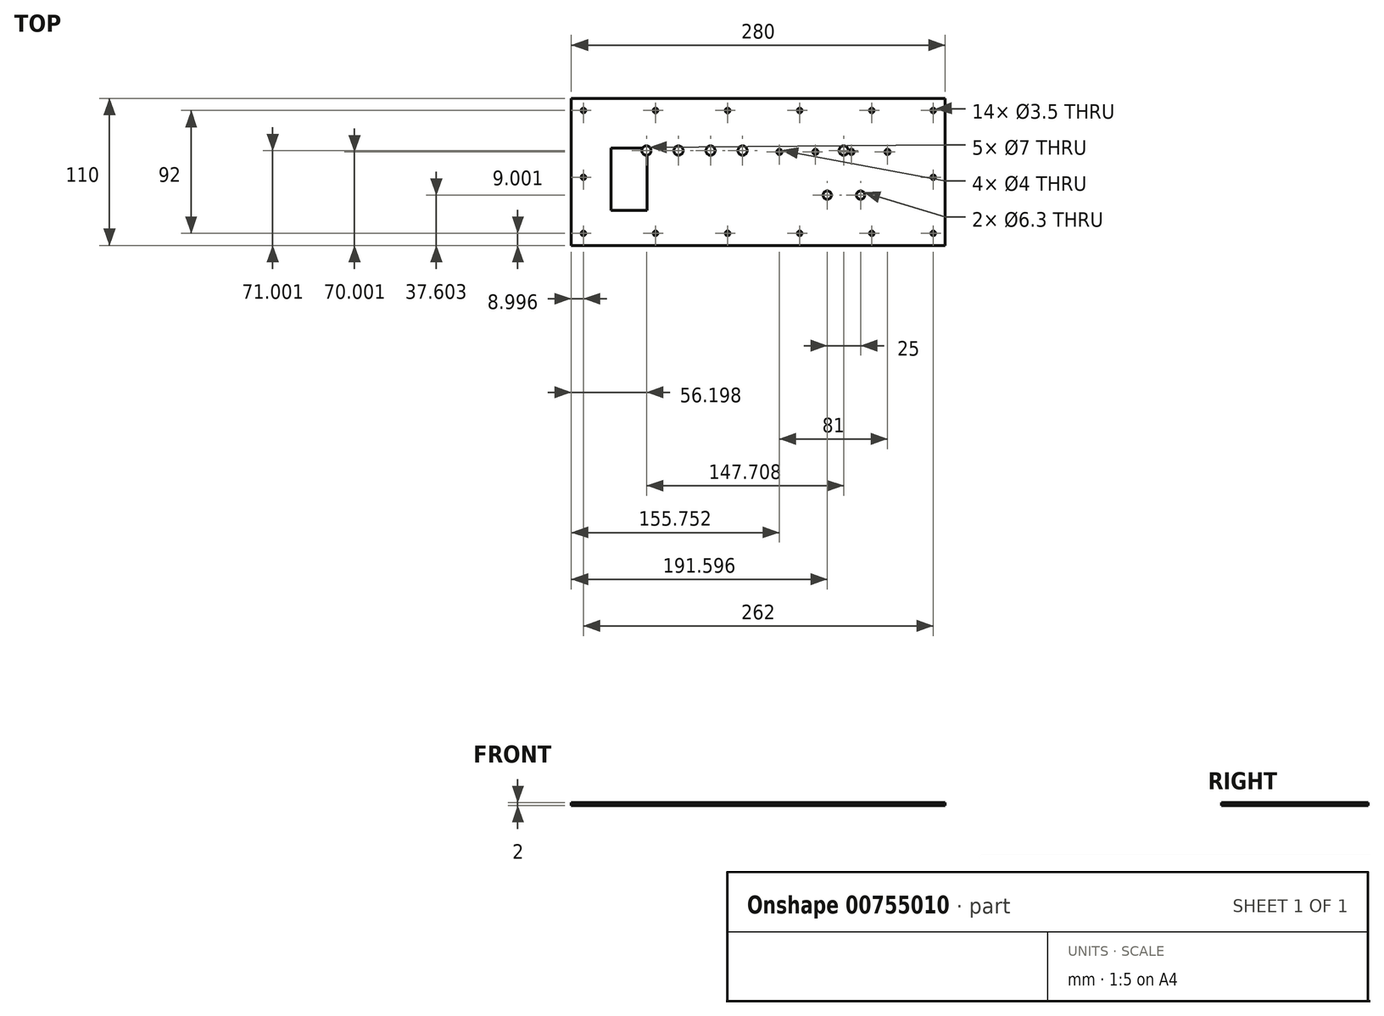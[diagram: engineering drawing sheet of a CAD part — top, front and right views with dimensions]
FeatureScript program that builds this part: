
annotation { "Feature Type Name" : "Feature", "Feature Type Description" : "" }
export const myFeature = defineFeature(function(context is Context, id is Id, definition is map)
    precondition{}
    {
        {
            var Q0;
            Q0=qCreatedBy(makeId("Top.planeOp"),FACE);
            var sketch = newSketch(context, id + "F0", { "sketchPlane" : qUnion([Q0])});
            skLineSegment(sketch, "E0.bottom", {"start": v(-230.24, 76.32) * mm, "end": v(49.76, 76.32) * mm});
            skLineSegment(sketch, "E0.top", {"start": v(-230.24, -33.68) * mm, "end": v(49.76, -33.68) * mm});
            skLineSegment(sketch, "E0.left", {"start": v(-230.24, 76.32) * mm, "end": v(-230.24, -33.68) * mm});
            skLineSegment(sketch, "E0.right", {"start": v(49.76, 76.32) * mm, "end": v(49.76, -33.68) * mm});
            skSolve(sketch);
        }
        {
            var Q0;
            Q0=makeQuery(id+"F0.imprint","IMPRINT",FACE,{"disambiguationData":[TD([[makeQuery(id+"F0.imprint","IMPRINT",EDGE,{"derivedFrom":sQuery(id+"F0.wireOp",EDGE,"E0.bottom")}),-1.0]])]});
            extrude(context, id + "F1", {"entities" : qUnion([Q0]), "depth" : 2 * mm, "offsetDistance" : 25 * mm});
        }
        {
            var Q0;
            Q0=makeQuery(id+"F1.opExtrude","CAP_FACE",FACE,{"disambiguationData":[OSD([sQuery(id+"F0.wireOp",EDGE,"E0.bottom"),sQuery(id+"F0.wireOp",EDGE,"E0.top"),sQuery(id+"F0.wireOp",EDGE,"E0.left"),sQuery(id+"F0.wireOp",EDGE,"E0.right")])],"isStart":false});
            var sketch = newSketch(context, id + "F2", { "sketchPlane" : qUnion([Q0])});
            skCircle(sketch, "E1", {"center": v(-174.04, 37.32) * mm, "radius": 3.5 * mm});
            skCircle(sketch, "E2.1.0.0", {"center": v(-150.04, 37.32) * mm, "radius": 3.5 * mm});
            skCircle(sketch, "E2.2.0.0", {"center": v(-126.04, 37.32) * mm, "radius": 3.5 * mm});
            skCircle(sketch, "E2.3.0.0", {"center": v(-102.04, 37.32) * mm, "radius": 3.5 * mm});
            skLineSegment(sketch, "E2.direction1", {"start": v(-174.04, 37.32) * mm, "end": v(-150.04, 37.32) * mm, "construction": true});
            skCircle(sketch, "E3", {"center": v(-26.33, 37.32) * mm, "radius": 3.5 * mm});
            skCircle(sketch, "E4", {"center": v(-13.64, 3.92) * mm, "radius": 3.15 * mm});
            skCircle(sketch, "E5.1.0.0", {"center": v(-38.64, 3.92) * mm, "radius": 3.15 * mm});
            skLineSegment(sketch, "E5.direction1", {"start": v(-13.64, 3.92) * mm, "end": v(-38.64, 3.92) * mm, "construction": true});
            skSolve(sketch);
        }
        {
            var Q0;
            Q0 = qSketchRegion(id + "F2", true);
            extrude(context, id + "F3", {"entities" : qUnion([Q0]), "operationType" : NewBodyOperationType.REMOVE, "oppositeDirection" : true, "depth" : 25 * mm, "offsetDistance" : 25 * mm});
        }
        {
            var Q0;
            Q0=makeQuery(id+"F1.opExtrude","CAP_FACE",FACE,{"disambiguationData":[OSD([sQuery(id+"F0.wireOp",EDGE,"E0.bottom"),sQuery(id+"F0.wireOp",EDGE,"E0.top"),sQuery(id+"F0.wireOp",EDGE,"E0.left"),sQuery(id+"F0.wireOp",EDGE,"E0.right")])],"isStart":true});
            var sketch = newSketch(context, id + "F4", { "sketchPlane" : qUnion([Q0])});
            skCircle(sketch, "E6", {"center": v(6.51, -36.32) * mm, "radius": 2 * mm});
            skCircle(sketch, "E7.1.0.0", {"center": v(-20.49, -36.32) * mm, "radius": 2 * mm});
            skCircle(sketch, "E7.2.0.0", {"center": v(-47.49, -36.32) * mm, "radius": 2 * mm});
            skCircle(sketch, "E7.3.0.0", {"center": v(-74.49, -36.32) * mm, "radius": 2 * mm});
            skLineSegment(sketch, "E7.direction1", {"start": v(6.51, -36.32) * mm, "end": v(-20.49, -36.32) * mm, "construction": true});
            skCircle(sketch, "E8", {"center": v(-221.24, 24.68) * mm, "radius": 1.75 * mm});
            skCircle(sketch, "E9", {"center": v(-221.24, -67.32) * mm, "radius": 1.75 * mm});
            skCircle(sketch, "E10", {"center": v(40.76, 24.68) * mm, "radius": 1.75 * mm});
            skCircle(sketch, "E11", {"center": v(40.76, -67.32) * mm, "radius": 1.75 * mm});
            skCircle(sketch, "E12.1.0.0", {"center": v(-167.24, 24.68) * mm, "radius": 1.75 * mm});
            skCircle(sketch, "E12.1.0.1", {"center": v(-167.24, -67.32) * mm, "radius": 1.75 * mm});
            skCircle(sketch, "E12.2.0.0", {"center": v(-113.24, 24.68) * mm, "radius": 1.75 * mm});
            skCircle(sketch, "E12.2.0.1", {"center": v(-113.24, -67.32) * mm, "radius": 1.75 * mm});
            skCircle(sketch, "E12.3.0.0", {"center": v(-59.24, 24.68) * mm, "radius": 1.75 * mm});
            skCircle(sketch, "E12.3.0.1", {"center": v(-59.24, -67.32) * mm, "radius": 1.75 * mm});
            skCircle(sketch, "E12.4.0.0", {"center": v(-5.24, 24.68) * mm, "radius": 1.75 * mm});
            skCircle(sketch, "E12.4.0.1", {"center": v(-5.24, -67.32) * mm, "radius": 1.75 * mm});
            skLineSegment(sketch, "E12.direction1", {"start": v(-221.24, -67.32) * mm, "end": v(-167.24, -67.32) * mm, "construction": true});
            skCircle(sketch, "E13.0.1.0", {"center": v(-221.24, -17.32) * mm, "radius": 1.75 * mm});
            skCircle(sketch, "E13.0.1.1", {"center": v(40.76, -17.32) * mm, "radius": 1.75 * mm});
            skLineSegment(sketch, "E13.direction1", {"start": v(-221.24, -67.32) * mm, "end": v(-196.24, -67.32) * mm, "construction": true});
            skLineSegment(sketch, "E13.direction2", {"start": v(-221.24, -67.32) * mm, "end": v(-221.24, -17.32) * mm, "construction": true});
            skSolve(sketch);
        }
        {
            var Q0;
            Q0 = qSketchRegion(id + "F4", true);
            extrude(context, id + "F5", {"entities" : qUnion([Q0]), "operationType" : NewBodyOperationType.REMOVE, "oppositeDirection" : true, "depth" : 25 * mm, "offsetDistance" : 25 * mm});
        }
        {
            var Q0;
            Q0=makeQuery(id+"F1.opExtrude","CAP_FACE",FACE,{"disambiguationData":[OSD([sQuery(id+"F0.wireOp",EDGE,"E0.bottom"),sQuery(id+"F0.wireOp",EDGE,"E0.top"),sQuery(id+"F0.wireOp",EDGE,"E0.left"),sQuery(id+"F0.wireOp",EDGE,"E0.right")])],"isStart":false});
            var sketch = newSketch(context, id + "F6", { "sketchPlane" : qUnion([Q0])});
            skLineSegment(sketch, "E14.bottom", {"start": v(-200.63, 39.32) * mm, "end": v(-173.43, 39.32) * mm});
            skLineSegment(sketch, "E14.top", {"start": v(-200.63, -7.38) * mm, "end": v(-173.43, -7.38) * mm});
            skLineSegment(sketch, "E14.left", {"start": v(-200.63, 39.32) * mm, "end": v(-200.63, -7.38) * mm});
            skLineSegment(sketch, "E14.right", {"start": v(-173.43, 39.32) * mm, "end": v(-173.43, -7.38) * mm});
            skSolve(sketch);
        }
        {
            var Q0;
            Q0 = qSketchRegion(id + "F6", true);
            extrude(context, id + "F7", {"entities" : qUnion([Q0]), "operationType" : NewBodyOperationType.REMOVE, "oppositeDirection" : true, "depth" : 1 * mm, "offsetDistance" : 25 * mm});
        }
    });
